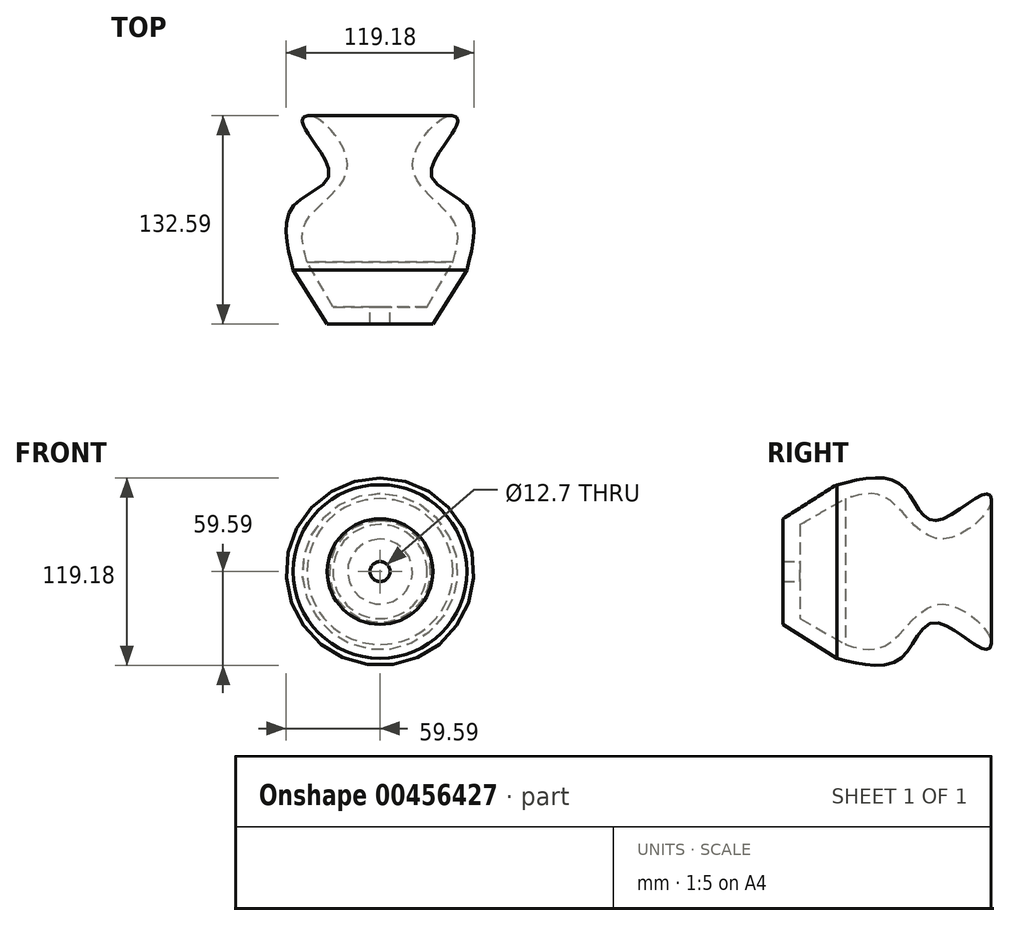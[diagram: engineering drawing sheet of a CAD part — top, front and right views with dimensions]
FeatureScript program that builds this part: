
annotation { "Feature Type Name" : "Feature", "Feature Type Description" : "" }
export const myFeature = defineFeature(function(context is Context, id is Id, definition is map)
    precondition{}
    {
        {
            var Q0;
            Q0=qCreatedBy(makeId("Top.planeOp"),FACE);
            var sketch = newSketch(context, id + "F0", { "sketchPlane" : qUnion([Q0])});
            skLineSegment(sketch, "E0", {"start": v(0, 75.44) * mm, "end": v(0, -77.27) * mm});
            skLineSegment(sketch, "E1", {"start": v(0, -68.43) * mm, "end": v(33.53, -68.43) * mm});
            skLineSegment(sketch, "E2", {"start": v(33.53, -68.43) * mm, "end": v(55.17, -34.1) * mm});
            skFitSpline(sketch, "E3", {"points": [v(55.17, -34.1) * mm, v(55.17, 6.55) * mm, v(32.3, 27.28) * mm, v(49.42, 60.4) * mm, v(43.28, 63.77) * mm, v(20.73, 30.63) * mm, v(46.94, -2.9) * mm, v(46.33, -28.8) * mm], "startDerivative": vector(69.01, 275.44) * mm, "endDerivative": vector(-56.52, -199.42) * mm});
            skLineSegment(sketch, "E4", {"start": v(46.33, -28.8) * mm, "end": v(29.87, -57.45) * mm});
            skLineSegment(sketch, "E5", {"start": v(29.87, -57.45) * mm, "end": v(0, -57.45) * mm});
            skSolve(sketch);
        }
        {
            var Q0;
            {var subQ0=sQuery(id+"F0.wireOp",EDGE,"E1");Q0=makeQuery(id+"F0.imprint","IMPRINT",FACE,{"disambiguationData":[TD([[makeQuery(id+"F0.imprint","IMPRINT",EDGE,{"derivedFrom":subQ0}),1.0]])]});}
            var Q1;
            Q1=sQuery(id+"F0.wireOp",EDGE,"E0");
            revolve(context, id + "F1", {"entities" : qUnion([Q0]), "axis" : qUnion([Q1]), "revolveType" : RevolveType.FULL});
        }
        {
            var Q0;
            Q0=qCreatedBy(makeId("Front.planeOp"),FACE);
            var sketch = newSketch(context, id + "F2", { "sketchPlane" : qUnion([Q0])});
            skPoint(sketch, "E6", {"position": v(0, 0) * mm});
            skSolve(sketch);
        }
        {
            var Q0;
            Q0=sQuery(id+"F2.wireOp",VERTEX,"E6");
            var Q1;
            Q1=makeQuery(id+"F1.opRevolve","SWEPT_BODY",BODY,{"disambiguationData":[OSD([sQuery(id+"F0.wireOp",EDGE,"E0"),sQuery(id+"F0.wireOp",EDGE,"E1"),sQuery(id+"F0.wireOp",EDGE,"E2"),sQuery(id+"F0.wireOp",EDGE,"E3"),sQuery(id+"F0.wireOp",EDGE,"E4"),sQuery(id+"F0.wireOp",EDGE,"E5")])]});
            hole(context, id + "F3", {"style" : HoleStyle.SIMPLE, "endStyle" : HoleEndStyle.THROUGH, "oppositeDirection" : true, "holeDiameter" : 12.7 * mm, "isTappedThrough" : true, "tappedDepth" : 12.7 * mm, "tapClearance" : 3, "locations" : qUnion([Q0]), "scope" : qUnion([Q1])});
        }
    });
